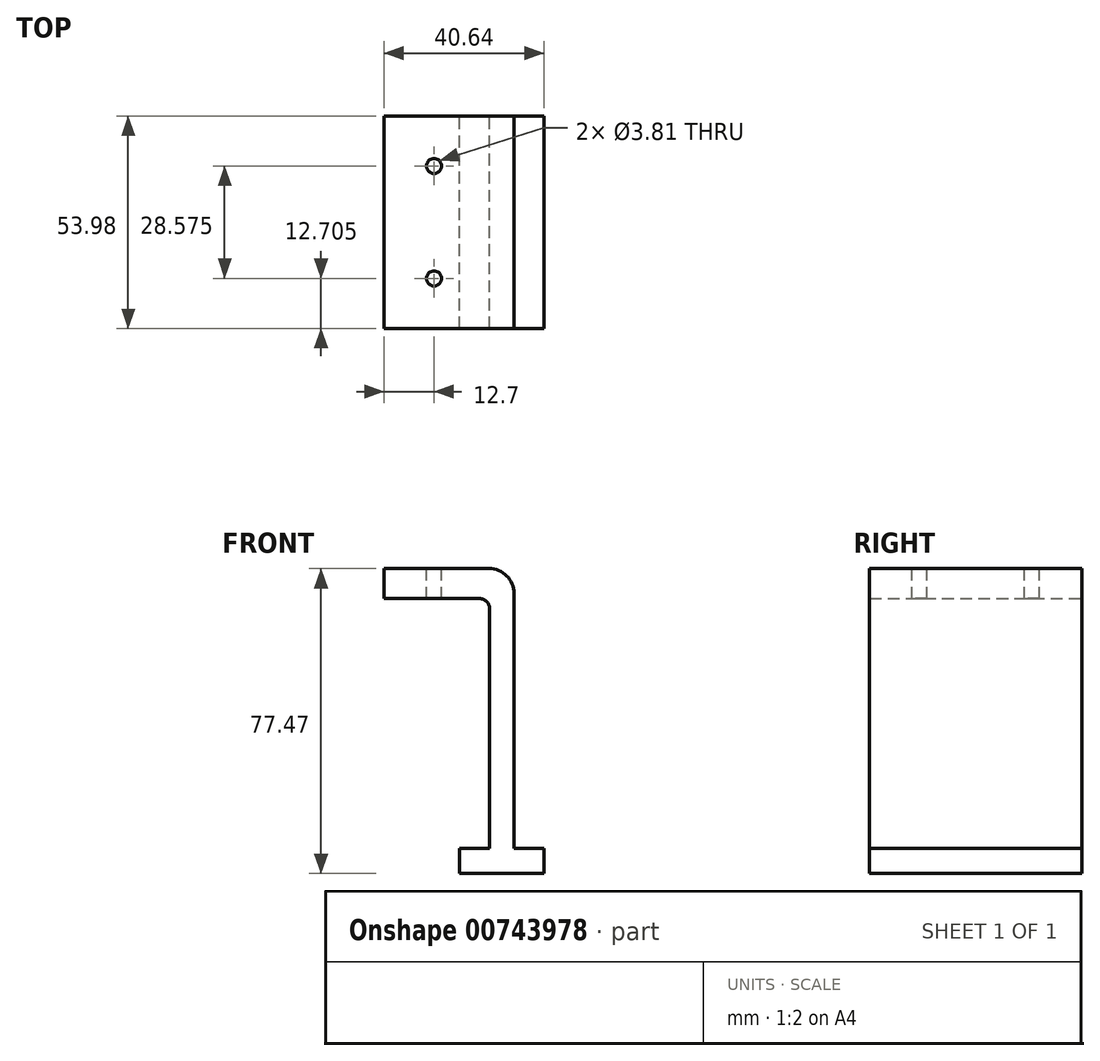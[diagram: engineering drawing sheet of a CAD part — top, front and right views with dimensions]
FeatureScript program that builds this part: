
annotation { "Feature Type Name" : "Feature", "Feature Type Description" : "" }
export const myFeature = defineFeature(function(context is Context, id is Id, definition is map)
    precondition{}
    {
        {
            var Q0;
            Q0=qCreatedBy(makeId("Front.planeOp"),FACE);
            var sketch = newSketch(context, id + "F0", { "sketchPlane" : qUnion([Q0])});
            skLineSegment(sketch, "E0", {"start": v(0, 0) * mm, "end": v(24.26, 0) * mm});
            skLineSegment(sketch, "E1", {"start": v(26.8, -2.54) * mm, "end": v(26.8, -63.5) * mm});
            skLineSegment(sketch, "E2", {"start": v(26.8, -63.5) * mm, "end": v(19.18, -63.5) * mm});
            skLineSegment(sketch, "E3", {"start": v(19.18, -63.5) * mm, "end": v(19.18, -69.85) * mm});
            skLineSegment(sketch, "E4", {"start": v(19.18, -69.85) * mm, "end": v(40.64, -69.85) * mm});
            skLineSegment(sketch, "E5", {"start": v(40.64, -69.85) * mm, "end": v(40.64, -63.5) * mm});
            skLineSegment(sketch, "E6", {"start": v(40.64, -63.5) * mm, "end": v(33.02, -63.5) * mm});
            skLineSegment(sketch, "E7", {"start": v(33.02, -63.5) * mm, "end": v(33.02, 1.27) * mm});
            skLineSegment(sketch, "E8", {"start": v(26.67, 7.62) * mm, "end": v(0, 7.62) * mm});
            skLineSegment(sketch, "E9", {"start": v(0, 7.62) * mm, "end": v(0, 0) * mm});
            skPoint(sketch, "E10.visualSharp", {"position": v(33.02, 7.62) * mm});
            skArc(sketch, "E10.filletArc", {"start": v(33.02, 1.27) * mm, "mid": v(31.16, 5.76) * mm, "end": v(26.67, 7.62) * mm});
            skPoint(sketch, "E11.visualSharp", {"position": v(26.8, 0) * mm});
            skArc(sketch, "E11.filletArc", {"start": v(26.8, -2.54) * mm, "mid": v(26.05, -0.74) * mm, "end": v(24.26, 0) * mm});
            skSolve(sketch);
        }
        {
            var Q0;
            Q0 = qSketchRegion(id + "F0", true);
            extrude(context, id + "F1", {"entities" : qUnion([Q0]), "depth" : 53.97 * mm, "offsetDistance" : 25.4 * mm});
        }
        {
            var Q0;
            Q0=makeQuery(id+"F1.opExtrude","SWEPT_FACE",FACE,{"disambiguationData":[OSD([sQuery(id+"F0.wireOp",EDGE,"E8")])]});
            var sketch = newSketch(context, id + "F2", { "sketchPlane" : qUnion([Q0])});
            skCircle(sketch, "E12", {"center": v(12.7, -41.27) * mm, "radius": 1.9 * mm});
            skCircle(sketch, "E13", {"center": v(12.7, -12.7) * mm, "radius": 1.9 * mm});
            skSolve(sketch);
        }
        {
            var Q0;
            Q0 = qSketchRegion(id + "F2", true);
            extrude(context, id + "F3", {"entities" : qUnion([Q0]), "operationType" : NewBodyOperationType.REMOVE, "oppositeDirection" : true, "depth" : 25.4 * mm, "offsetDistance" : 25.4 * mm});
        }
    });
